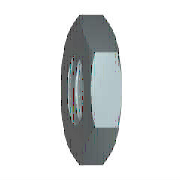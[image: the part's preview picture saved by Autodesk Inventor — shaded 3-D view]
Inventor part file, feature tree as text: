
AUTODESK INVENTOR PART (.ipt)
format: ipt  version: 2017 (Build 210142000, 142)  size: 162,816 bytes
history: native  units: mm (DEFAULTED — no unit token found)
features: sketch x3, other x2, extrude x1, hole x1, plane x1
ambient origin geometry x7: Origin, YZ Plane, XZ Plane, X Axis, Y Axis, Z Axis, Center Point
bodies: Solid1 (feature_tree)
feature tree (8):
  extrude  "Corps"  Depth=6.350853mm
  other  "Chanfrein1"
  hole  "Filetage"  [1 undecoded]
  other  "Work Axis1"
  plane  "Work Plane1"
  sketch  "Esquisse1"
  sketch  "Esquisse2"
  sketch  "Esquisse3"
note: 1 required parameter value undecoded (feature->parameter linkage not recoverable at this tier; creation-order binding heuristic only, values carry confidence <= 0.55)
